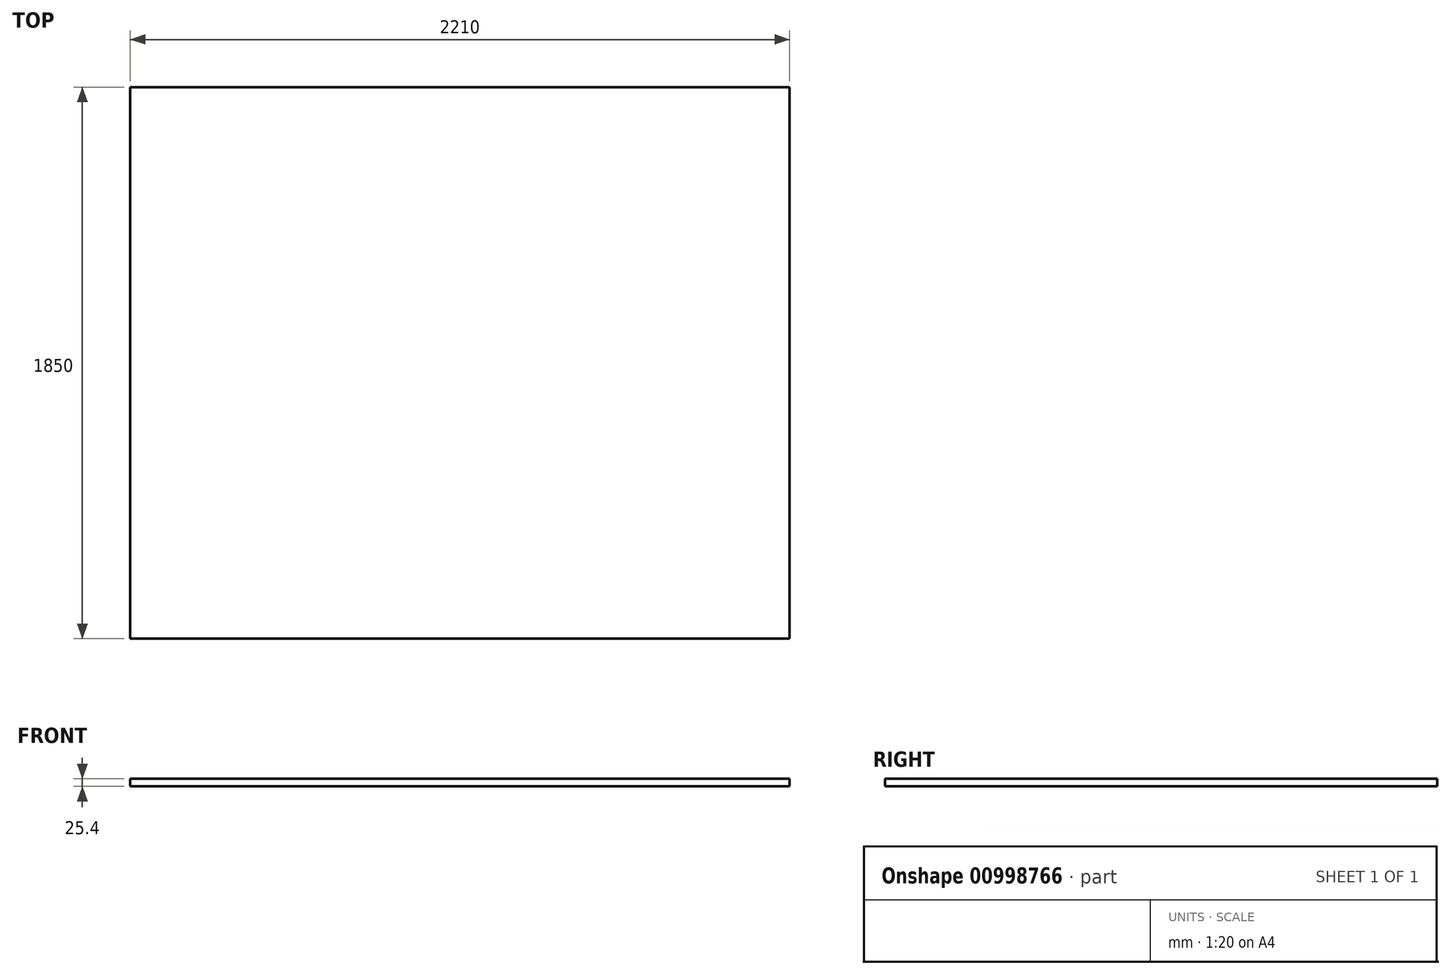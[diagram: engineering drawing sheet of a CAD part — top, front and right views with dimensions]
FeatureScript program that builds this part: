
annotation { "Feature Type Name" : "Feature", "Feature Type Description" : "" }
export const myFeature = defineFeature(function(context is Context, id is Id, definition is map)
    precondition{}
    {
        {
            var Q0;
            Q0=qCreatedBy(makeId("Top.planeOp"),FACE);
            var sketch = newSketch(context, id + "F0", { "sketchPlane" : qUnion([Q0])});
            skLineSegment(sketch, "E0.bottom", {"start": v(-2806.78, 974.83) * mm, "end": v(-596.78, 974.83) * mm});
            skLineSegment(sketch, "E0.top", {"start": v(-2806.78, -875.17) * mm, "end": v(-596.78, -875.17) * mm});
            skLineSegment(sketch, "E0.left", {"start": v(-2806.78, 974.83) * mm, "end": v(-2806.78, -875.17) * mm});
            skLineSegment(sketch, "E0.right", {"start": v(-596.78, 974.83) * mm, "end": v(-596.78, -875.17) * mm});
            skSolve(sketch);
        }
        {
            var Q0;
            Q0=makeQuery(id+"F0.imprint","IMPRINT",FACE,{"disambiguationData":[TD([[makeQuery(id+"F0.imprint","IMPRINT",EDGE,{"derivedFrom":sQuery(id+"F0.wireOp",EDGE,"E0.bottom")}),-1.0]])]});
            extrude(context, id + "F1", {"entities" : qUnion([Q0]), "depth" : -25.4 * mm, "offsetDistance" : 25.4 * mm});
        }
    });
